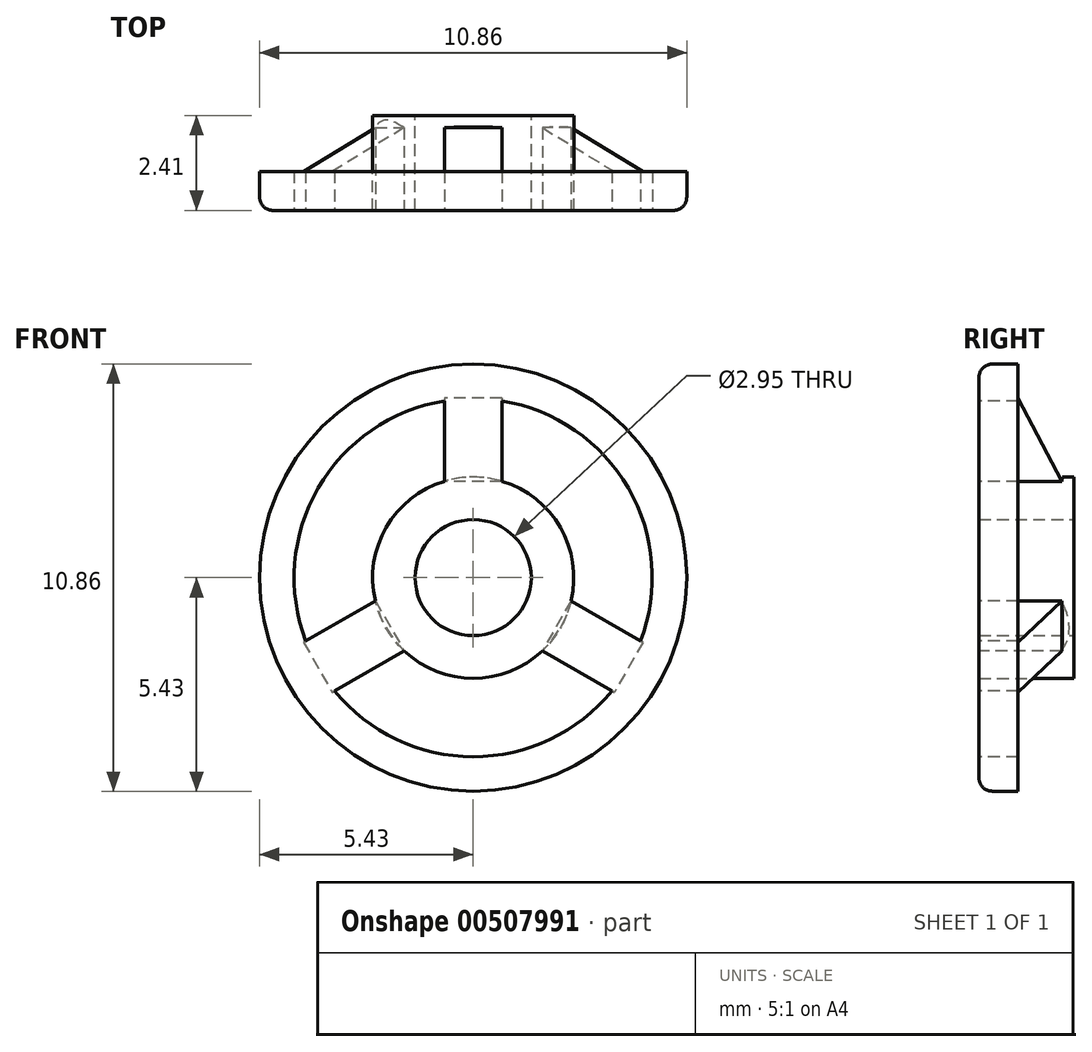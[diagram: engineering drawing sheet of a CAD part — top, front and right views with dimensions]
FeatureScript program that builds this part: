
annotation { "Feature Type Name" : "Feature", "Feature Type Description" : "" }
export const myFeature = defineFeature(function(context is Context, id is Id, definition is map)
    precondition{}
    {
        {
            var Q0;
            Q0=qCreatedBy(makeId("Front.planeOp"),FACE);
            var sketch = newSketch(context, id + "F0", { "sketchPlane" : qUnion([Q0])});
            skCircle(sketch, "E0", {"center": v(0, 0) * mm, "radius": 2.56 * mm});
            skCircle(sketch, "E1", {"center": v(0, 0) * mm, "radius": 1.48 * mm});
            skSolve(sketch);
        }
        {
            var Q0;
            Q0 = qSketchRegion(id + "F0", true);
            extrude(context, id + "F1", {"entities" : qUnion([Q0]), "depth" : 2.41 * mm});
        }
        {
            var Q0;
            Q0=makeQuery(id+"F1.opExtrude","CAP_FACE",FACE,{"disambiguationData":[OSD([sQuery(id+"F0.wireOp",EDGE,"E0"),sQuery(id+"F0.wireOp",EDGE,"E1")])],"isStart":false});
            var sketch = newSketch(context, id + "F2", { "sketchPlane" : qUnion([Q0])});
            skLineSegment(sketch, "E2", {"start": v(-0.73, 2.45) * mm, "end": v(-0.73, 4.56) * mm});
            skLineSegment(sketch, "E3", {"start": v(0.73, 2.45) * mm, "end": v(0.73, 4.56) * mm});
            skLineSegment(sketch, "E4", {"start": v(-0.73, 4.56) * mm, "end": v(0.73, 4.56) * mm});
            skLineSegment(sketch, "E5", {"start": v(-0.73, 2.45) * mm, "end": v(0.73, 2.45) * mm});
            skLineSegment(sketch, "E6.1.0", {"start": v(-1.76, -1.86) * mm, "end": v(-2.49, -0.6) * mm});
            skLineSegment(sketch, "E6.1.1", {"start": v(-3.58, -2.91) * mm, "end": v(-4.31, -1.65) * mm});
            skLineSegment(sketch, "E6.1.2", {"start": v(-1.76, -1.86) * mm, "end": v(-3.58, -2.91) * mm});
            skLineSegment(sketch, "E6.1.3", {"start": v(-2.49, -0.6) * mm, "end": v(-4.31, -1.65) * mm});
            skLineSegment(sketch, "E6.2.0", {"start": v(2.49, -0.6) * mm, "end": v(1.76, -1.86) * mm});
            skLineSegment(sketch, "E6.2.1", {"start": v(4.31, -1.65) * mm, "end": v(3.58, -2.91) * mm});
            skLineSegment(sketch, "E6.2.2", {"start": v(2.49, -0.6) * mm, "end": v(4.31, -1.65) * mm});
            skLineSegment(sketch, "E6.2.3", {"start": v(1.76, -1.86) * mm, "end": v(3.58, -2.91) * mm});
            skPoint(sketch, "E6.center", {"position": v(0, 0) * mm});
            skSolve(sketch);
        }
        {
            var Q0;
            Q0 = qSketchRegion(id + "F2", true);
            extrude(context, id + "F3", {"entities" : qUnion([Q0]), "operationType" : NewBodyOperationType.ADD, "oppositeDirection" : true, "depth" : 2.1 * mm});
        }
        {
            var Q0;
            Q0=makeQuery(id+"F3.opExtrude","SWEPT_FACE",FACE,{"disambiguationData":[OSD([sQuery(id+"F2.wireOp",EDGE,"E6.2.3")])]});
            var sketch = newSketch(context, id + "F4", { "sketchPlane" : qUnion([Q0])});
            skLineSegment(sketch, "E7", {"start": v(2.45, 0.3) * mm, "end": v(3.48, 0.08) * mm});
            skLineSegment(sketch, "E8", {"start": v(3.48, 0.08) * mm, "end": v(4.9, 0.21) * mm});
            skLineSegment(sketch, "E9", {"start": v(4.9, 0.21) * mm, "end": v(4.9, 2.57) * mm});
            skLineSegment(sketch, "E10", {"start": v(2.45, 0.31) * mm, "end": v(4.56, 1.42) * mm});
            skLineSegment(sketch, "E11", {"start": v(4.56, 1.42) * mm, "end": v(4.71, 1.64) * mm});
            skLineSegment(sketch, "E12", {"start": v(4.71, 1.64) * mm, "end": v(4.71, 2.48) * mm});
            skLineSegment(sketch, "E13", {"start": v(4.71, 2.48) * mm, "end": v(4.9, 2.57) * mm});
            skSolve(sketch);
        }
        {
            var Q0;
            Q0 = qSketchRegion(id + "F4", true);
            extrude(context, id + "F5", {"entities" : qUnion([Q0]), "operationType" : NewBodyOperationType.REMOVE, "oppositeDirection" : true, "depth" : 25 * mm});
        }
        {
            var Q0;
            Q0=makeQuery(id+"F3.opExtrude","SWEPT_FACE",FACE,{"disambiguationData":[OSD([sQuery(id+"F2.wireOp",EDGE,"E2")])]});
            var sketch = newSketch(context, id + "F6", { "sketchPlane" : qUnion([Q0])});
            skLineSegment(sketch, "E14", {"start": v(0.31, 2.45) * mm, "end": v(0.1, 3.52) * mm});
            skLineSegment(sketch, "E15", {"start": v(0.1, 3.52) * mm, "end": v(0.2, 5.02) * mm});
            skLineSegment(sketch, "E16", {"start": v(0.2, 5.02) * mm, "end": v(2.41, 4.74) * mm});
            skPoint(sketch, "E17", {"position": v(1.42, 4.56) * mm});
            skLineSegment(sketch, "E18", {"start": v(1.42, 4.56) * mm, "end": v(0.3, 2.45) * mm});
            skLineSegment(sketch, "E19", {"start": v(1.42, 4.56) * mm, "end": v(2.41, 4.74) * mm});
            skSolve(sketch);
        }
        {
            var Q0;
            Q0 = qSketchRegion(id + "F6", true);
            extrude(context, id + "F7", {"entities" : qUnion([Q0]), "operationType" : NewBodyOperationType.REMOVE, "oppositeDirection" : true, "depth" : 25 * mm});
        }
        {
            var Q0;
            Q0=makeQuery(id+"F3.opExtrude","SWEPT_FACE",FACE,{"disambiguationData":[OSD([sQuery(id+"F2.wireOp",EDGE,"E6.1.2")])]});
            var sketch = newSketch(context, id + "F8", { "sketchPlane" : qUnion([Q0])});
            skLineSegment(sketch, "E20", {"start": v(-5.5, 1.44) * mm, "end": v(-4.84, -0.1) * mm});
            skLineSegment(sketch, "E21", {"start": v(-4.84, -0.1) * mm, "end": v(-2.67, -0.1) * mm});
            skLineSegment(sketch, "E22", {"start": v(-2.67, -0.1) * mm, "end": v(-2.45, 0.3) * mm});
            skLineSegment(sketch, "E23", {"start": v(-2.45, 0.3) * mm, "end": v(-4.56, 1.42) * mm});
            skLineSegment(sketch, "E24", {"start": v(-4.56, 1.42) * mm, "end": v(-5.5, 1.44) * mm});
            skSolve(sketch);
        }
        {
            var Q0;
            Q0 = qSketchRegion(id + "F8", true);
            extrude(context, id + "F9", {"entities" : qUnion([Q0]), "operationType" : NewBodyOperationType.REMOVE, "oppositeDirection" : true, "depth" : 25 * mm});
        }
        {
            var Q0;
            Q0=makeQuery(id+"F3.boolean.opBoolean","MERGE",FACE,{"derivedFrom":[makeQuery(id+"F1.opExtrude","CAP_FACE",FACE,{"disambiguationData":[OSD([sQuery(id+"F0.wireOp",EDGE,"E0"),sQuery(id+"F0.wireOp",EDGE,"E1")])],"isStart":false}),makeQuery(id+"F3.opExtrude","CAP_FACE",FACE,{"disambiguationData":[OSD([sQuery(id+"F2.wireOp",EDGE,"E2"),sQuery(id+"F2.wireOp",EDGE,"E3"),sQuery(id+"F2.wireOp",EDGE,"E4"),sQuery(id+"F2.wireOp",EDGE,"E5")])],"isStart":true}),makeQuery(id+"F3.opExtrude","CAP_FACE",FACE,{"disambiguationData":[OSD([sQuery(id+"F2.wireOp",EDGE,"E6.1.0"),sQuery(id+"F2.wireOp",EDGE,"E6.1.1"),sQuery(id+"F2.wireOp",EDGE,"E6.1.2"),sQuery(id+"F2.wireOp",EDGE,"E6.1.3")])],"isStart":true}),makeQuery(id+"F3.opExtrude","CAP_FACE",FACE,{"disambiguationData":[OSD([sQuery(id+"F2.wireOp",EDGE,"E6.2.0"),sQuery(id+"F2.wireOp",EDGE,"E6.2.1"),sQuery(id+"F2.wireOp",EDGE,"E6.2.2"),sQuery(id+"F2.wireOp",EDGE,"E6.2.3")])],"isStart":true})]});
            var sketch = newSketch(context, id + "F10", { "sketchPlane" : qUnion([Q0])});
            skCircle(sketch, "E25", {"center": v(0, 0) * mm, "radius": 4.55 * mm});
            skCircle(sketch, "E26", {"center": v(0, 0) * mm, "radius": 5.42 * mm});
            skSolve(sketch);
        }
        {
            var Q0;
            Q0 = qSketchRegion(id + "F10", true);
            extrude(context, id + "F11", {"entities" : qUnion([Q0]), "operationType" : NewBodyOperationType.ADD, "oppositeDirection" : true, "depth" : 0.99 * mm});
        }
        {
            var Q0;
            Q0=makeQuery(id+"F11.opExtrude","CAP_EDGE",EDGE,{"disambiguationData":[OSD([sQuery(id+"F10.wireOp",EDGE,"E26")])],"isStart":true});
            fillet(context, id + "F12", {"entities" : qUnion([Q0]), "radius" : 0.34 * mm, "tangentPropagation" : true, "allowEdgeOverflow" : false});
        }
    });
